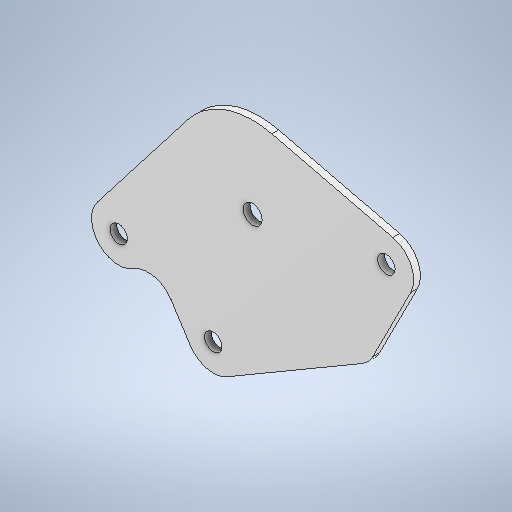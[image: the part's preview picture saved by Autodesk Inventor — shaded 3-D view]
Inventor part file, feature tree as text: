
AUTODESK INVENTOR PART (.ipt)
format: ipt  version: 2025.2 (Build 292293000, 293)  size: 267,264 bytes
history: native  units: in
note: dims shown in document units (in); Inventor stores cm internally (conversion verified against a paired STEP export)
features: other x5, sketch x2, plane x1, sheet_metal_op x1, extrude x1, reference x1
ambient origin geometry x8: Origin, YZ Plane, XZ Plane, XY Plane, X Axis, Y Axis, Z Axis, Center Point
bodies: Body1 (feature_tree)
feature tree (11):
  plane  "Work Plane1"
  sheet_metal_op  "Face3"
  extrude  "Extrusion1"  Depth=0.16in
  sketch  "Sketch1"  dims[d1=0.5in d14=0.16in]
  reference  "Reference3"
  other  "Plate3"
  sketch  "Sketch2"  dims[d15=0.0625in d16=0.175in d17=0.175in d18=1.5in d19=0.0in]
  parser-record x1  (decoder bookkeeping rows leaked as tree rows — omitted from the tree; the rows remain in map.json)
  other  "ACE 2.0.iam"
  other  "V5 Rotation Sensor:4"
  other  "Rear Vertical Odom Pod Rot Side:2"
note: 1 file-system path scrubbed to <path> (originals preserved in map.json)
